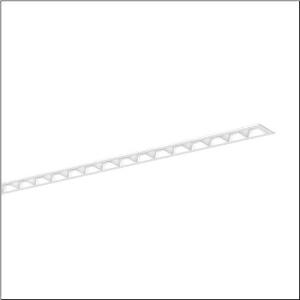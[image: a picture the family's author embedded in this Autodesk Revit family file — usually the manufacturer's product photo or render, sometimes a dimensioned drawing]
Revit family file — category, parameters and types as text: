
# Revit family: silica_r__21_51mx16db35wb_6bb0
name_source: partatom
category: Lighting Fixtures
units: mm (PartAtom-declared; Revit-internal decimal feet)

## family parameters
Cut with Voids When Loaded = No
Host = Face
Light Source = No
Part Type = Normal
Room Calculation Point = No
Round Connector Dimension = Use Diameter
Shared = No

## types (1)
- --- (1 x LED, 5400 lm, 31.4 W, 3000K)
    Apparent Load = 31 VA
    CIE Flux Codes = 83 98 100 100 100
    Color Rendering = 80
    Color Temperature = 3000K
    Default Elevation = 1800 mm
    Description = Silica® 21, office luminaire, primary light control with darklight reflector, of PMMA, white, CAT 2 (L<= 3000cd/m²), light emission: direct distribution, primary light characteristic: symmetric, installation type: recessed, LED, rated luminous flux: 5.400lm, luminous efficacy: 172lm/W, light colour: 830, colour temperature: 3000K, with terminal, 3+2-pole, max. 2.5mm², mains connection: 220..240V, AC, 50/60Hz, rated input power: 31.4W, luminaire housing, of aluminium, traffic white (RAL 9016), length: 1.528mm, width: 79mm, height: 53mm, protection rating (complete): IP20, insulation class (complete): insulation class I (protective earthing), certification: CE, permissible operating ambient temperature: 0..+35°C, standard: EN 50419, packaging unit: 1 piece
    Height = 0 mm  [stored 0 ft]
    Lamp = 1 x LED
    Lamp Light Flux = 5400 lm
    Lamp Power = 31.4 W
    Lamp count = 1
    Length = 1527 mm
    Luminous efficacy = 172 lm/W
    Manufacturer = Siteco
    ModVariant = No
    Model = 51MX16DB35WB
    Mounting Place = Ceiling
    Mounting Type = Recessed
    Number of Poles = 1
    OnlyDefault = Yes
    Power Factor = 1
    Product Name = Silica® 21
    Product group = office luminaire | ceiling recessed
    ProductGroupID = 401
    Protection Class = Protection class I
    Protection Degree = IP 20
    RLX_Detail_Level = 1
    RLX_Emergency_Light_Flux = 0 lm
    RLX_Emergency_Type = 0
    RLX_Emergency_Type_DB = No
    RlxData = <blob elided: 39457 chars, md5=6fdcaa60>
    Socket = socket
    Standby Power = 0 W
    System Light Flux = 5400 lm
    System Power = 31 W
    Type Comments = factory setting: luminous flux: 100 % | dim-lin: 254 | 360 mA
    Type Image = l_1313606.jpg
    URL = http://relux.com
    VarID = @adj_073273
    Voltage = 0 V
    Weight = 0.00 kg
    Width = 79 mm

note: [stored X ft] marks values corroborated as IEEE doubles in the binary element streams (Revit-internal decimal feet)

## geometry (parser evidence)
native form markers: Blend x4, Sweep x11
no freeform markers — native parametric forms only
